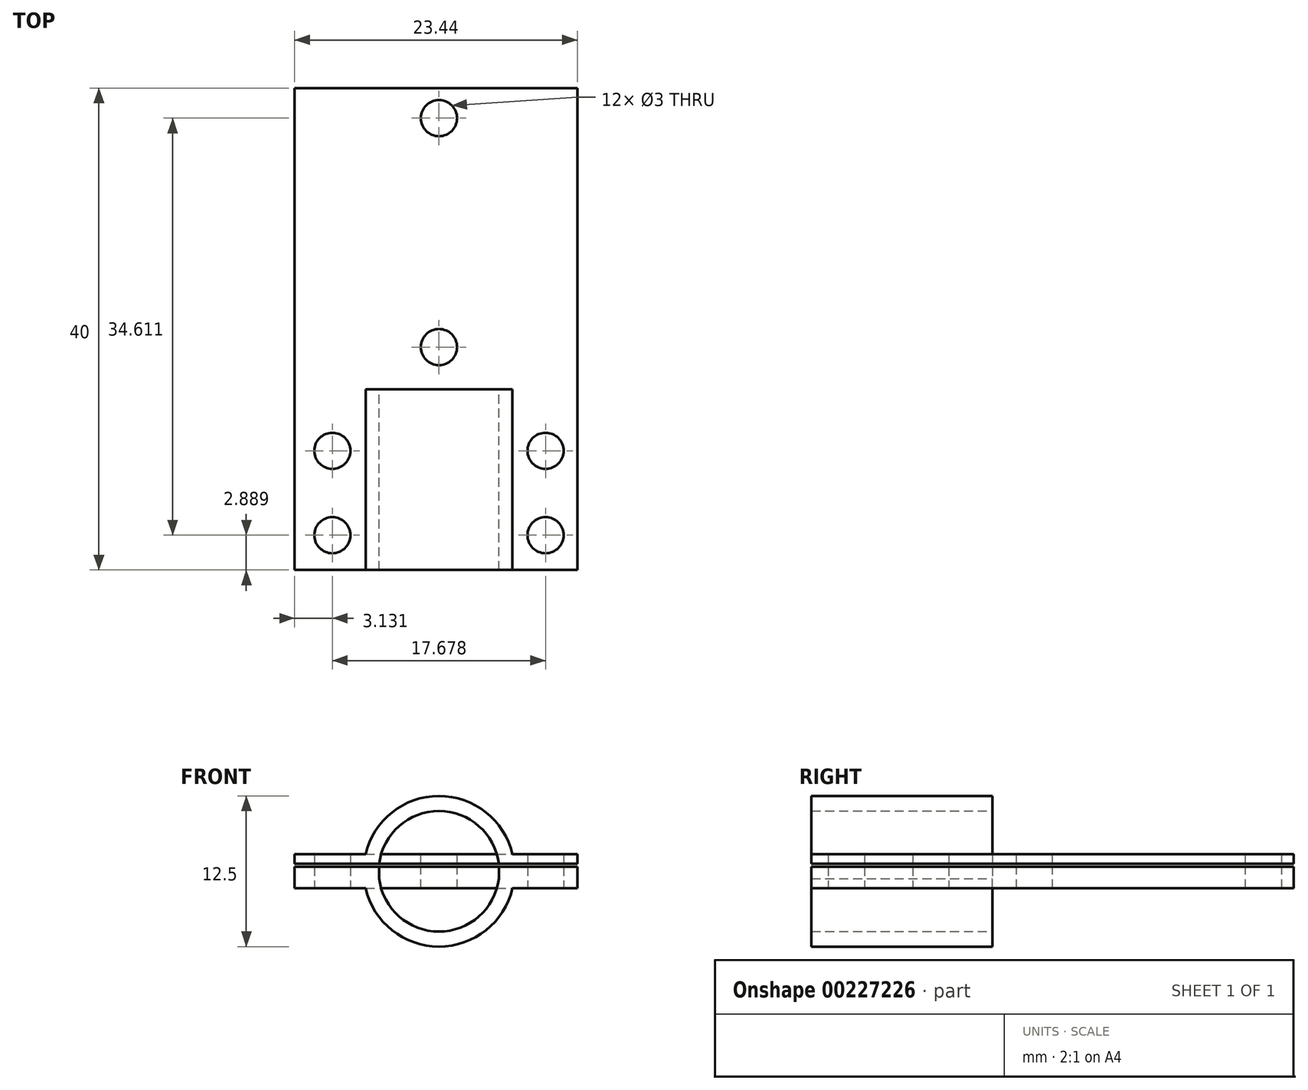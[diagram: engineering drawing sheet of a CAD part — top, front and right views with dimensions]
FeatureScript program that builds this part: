
annotation { "Feature Type Name" : "Feature", "Feature Type Description" : "" }
export const myFeature = defineFeature(function(context is Context, id is Id, definition is map)
    precondition{}
    {
        {
            var Q0;
            Q0=qCreatedBy(makeId("Front.planeOp"),FACE);
            var sketch = newSketch(context, id + "F0", { "sketchPlane" : qUnion([Q0])});
            skCircle(sketch, "E0", {"center": v(0, 0) * mm, "radius": 5 * mm});
            skArc(sketch, "E1", {"start": v(-6.09, -1.4) * mm, "mid": v(0, -6.25) * mm, "end": v(6.09, -1.4) * mm});
            skLineSegment(sketch, "E2.bottom", {"start": v(9.47, -1.4) * mm, "end": v(4.8, -1.4) * mm});
            skLineSegment(sketch, "E2.top", {"start": v(9.47, 1.4) * mm, "end": v(4.8, 1.4) * mm});
            skLineSegment(sketch, "E2.left", {"start": v(9.47, -1.4) * mm, "end": v(9.47, 1.4) * mm});
            skLineSegment(sketch, "E2.right", {"start": v(-9.47, -1.4) * mm, "end": v(-9.47, 1.4) * mm});
            skArc(sketch, "E3.trimOffspring", {"start": v(6.09, 1.4) * mm, "mid": v(0, 6.25) * mm, "end": v(-6.09, 1.4) * mm});
            skLineSegment(sketch, "E4.bottom", {"start": v(8.3, -0.63) * mm, "end": v(4.96, -0.63) * mm});
            skLineSegment(sketch, "E4.top", {"start": v(8.3, 0.63) * mm, "end": v(4.96, 0.63) * mm});
            skLineSegment(sketch, "E4.left", {"start": v(8.3, -0.63) * mm, "end": v(8.3, 0.63) * mm});
            skLineSegment(sketch, "E4.right", {"start": v(-8.3, -0.63) * mm, "end": v(-8.3, 0.63) * mm});
            skLineSegment(sketch, "E5.trimOffspring", {"start": v(-4.8, 1.4) * mm, "end": v(-9.47, 1.4) * mm});
            skLineSegment(sketch, "E6.trimOffspring", {"start": v(-4.96, 0.63) * mm, "end": v(-8.3, 0.63) * mm});
            skLineSegment(sketch, "E7.trimOffspring", {"start": v(-4.96, -0.63) * mm, "end": v(-8.3, -0.63) * mm});
            skLineSegment(sketch, "E8.trimOffspring", {"start": v(-4.8, -1.4) * mm, "end": v(-9.47, -1.4) * mm});
            skSolve(sketch);
        }
        {
            var Q0;
            Q0 = qSketchRegion(id + "F0", true);
            extrude(context, id + "F1", {"entities" : qUnion([Q0]), "endBound" : BoundingType.SYMMETRIC, "depth" : 25 * mm});
        }
        {
            var Q0;
            Q0=makeQuery(id+"F1.opExtrude","SWEPT_FACE",FACE,{"disambiguationData":[OSD([sQuery(id+"F0.wireOp",EDGE,"E5.trimOffspring")])]});
            var sketch = newSketch(context, id + "F2", { "sketchPlane" : qUnion([Q0])});
            skLineSegment(sketch, "E9", {"start": v(-9.47, 0) * mm, "end": v(9.47, 0) * mm});
            skPoint(sketch, "E9.endSnap0", {"position": v(-9.47, 0) * mm});
            skLineSegment(sketch, "E10", {"start": v(9.47, 0) * mm, "end": v(9.47, 12.5) * mm});
            skLineSegment(sketch, "E11", {"start": v(9.47, 12.5) * mm, "end": v(-9.47, 12.5) * mm});
            skLineSegment(sketch, "E12", {"start": v(-9.47, 12.5) * mm, "end": v(-9.47, 0) * mm});
            skSolve(sketch);
        }
        {
            var Q0;
            Q0 = qSketchRegion(id + "F2", true);
            extrude(context, id + "F3", {"entities" : qUnion([Q0]), "operationType" : NewBodyOperationType.ADD, "depth" : 5.1 * mm});
        }
        {
            var Q0;
            {var subQ3=sQuery(id+"F2.wireOp",EDGE,"E9");Q0=makeQuery(id+"F3.boolean.opBoolean","SPLIT",FACE,{"disambiguationData":[TD([makeQuery(id+"F3.opExtrude","CAP_FACE",FACE,{"disambiguationData":[OSD([subQ3,sQuery(id+"F2.wireOp",EDGE,"E10"),sQuery(id+"F2.wireOp",EDGE,"E11"),sQuery(id+"F2.wireOp",EDGE,"E12")])],"isStart":true})])],"derivedFrom":makeQuery(id+"F3.opExtrude","SWEPT_FACE",FACE,{"disambiguationData":[OSD([subQ3])]})});}
            extrude(context, id + "F4", {"entities" : qUnion([Q0]), "operationType" : NewBodyOperationType.REMOVE, "oppositeDirection" : true, "depth" : 25 * mm});
        }
        {
            var Q0;
            Q0=makeQuery(id+"F3.opExtrude","CAP_FACE",FACE,{"disambiguationData":[OSD([sQuery(id+"F2.wireOp",EDGE,"E9"),sQuery(id+"F2.wireOp",EDGE,"E10"),sQuery(id+"F2.wireOp",EDGE,"E11"),sQuery(id+"F2.wireOp",EDGE,"E12")])],"isStart":false});
            extrude(context, id + "F5", {"entities" : qUnion([Q0]), "operationType" : NewBodyOperationType.ADD, "oppositeDirection" : true, "depth" : 13 * mm});
        }
        {
            var Q0;
            {var subQ6=sQuery(id+"F0.wireOp",EDGE,"E4.bottom");var subQ9=sQuery(id+"F2.wireOp",EDGE,"E9");Q0=makeQuery(id+"F5.boolean.opBoolean","SPLIT",FACE,{"disambiguationData":[TD([makeQuery(id+"F1.opExtrude","SWEPT_FACE",FACE,{"disambiguationData":[OSD([subQ6])]})])],"derivedFrom":makeQuery(id+"F5.opExtrude","SWEPT_FACE",FACE,{"disambiguationData":[OSD([subQ9])]})});}
            extrude(context, id + "F6", {"entities" : qUnion([Q0]), "operationType" : NewBodyOperationType.REMOVE, "oppositeDirection" : true, "depth" : 3 * mm});
        }
        {
            var Q0;
            Q0=makeQuery(id+"F1.opExtrude","SWEPT_FACE",FACE,{"disambiguationData":[OSD([sQuery(id+"F0.wireOp",EDGE,"E2.bottom")])]});
            var sketch = newSketch(context, id + "F7", { "sketchPlane" : qUnion([Q0])});
            skCircle(sketch, "E13", {"center": v(8.84, 9.61) * mm, "radius": 1.5 * mm});
            skCircle(sketch, "E14.0.1.0", {"center": v(8.84, 2.61) * mm, "radius": 1.5 * mm});
            skLineSegment(sketch, "E14.direction1", {"start": v(8.84, 9.61) * mm, "end": v(33.84, 9.61) * mm, "construction": true});
            skLineSegment(sketch, "E14.direction2", {"start": v(8.84, 9.61) * mm, "end": v(8.84, 2.61) * mm, "construction": true});
            skCircle(sketch, "E15.MirrorC", {"center": v(-8.84, 9.61) * mm, "radius": 1.5 * mm});
            skCircle(sketch, "E16.MirrorC", {"center": v(-8.84, 2.61) * mm, "radius": 1.5 * mm});
            skSolve(sketch);
        }
        {
            var Q0;
            Q0=makeQuery(id+"F1.opExtrude","SWEPT_FACE",FACE,{"disambiguationData":[OSD([sQuery(id+"F0.wireOp",EDGE,"E2.left")])]});
            extrude(context, id + "F8", {"entities" : qUnion([Q0]), "operationType" : NewBodyOperationType.ADD, "depth" : 2 * mm});
        }
        {
            var Q0;
            {var subQ0=sQuery(id+"F0.wireOp",EDGE,"E4.left");Q0=makeQuery(id+"F6.boolean.opBoolean","MERGE",FACE,{"derivedFrom":[makeQuery(id+"F1.opExtrude","SWEPT_FACE",FACE,{"disambiguationData":[OSD([subQ0])]}),makeQuery(id+"F6.opExtrude","SWEPT_FACE",FACE,{"disambiguationData":[OSD([subQ0,sQuery(id+"F2.wireOp",EDGE,"E9")])]})]});}
            extrude(context, id + "F9", {"entities" : qUnion([Q0]), "operationType" : NewBodyOperationType.REMOVE, "oppositeDirection" : true, "depth" : 23.6 * mm});
        }
        {
            var Q0;
            {var subQ0=sQuery(id+"F2.wireOp",EDGE,"E12");Q0=makeQuery(id+"F5.boolean.opBoolean","MERGE",FACE,{"derivedFrom":[makeQuery(id+"F3.boolean.opBoolean","MERGE",FACE,{"derivedFrom":[makeQuery(id+"F1.opExtrude","SWEPT_FACE",FACE,{"disambiguationData":[OSD([sQuery(id+"F0.wireOp",EDGE,"E2.right")])]}),makeQuery(id+"F3.opExtrude","SWEPT_FACE",FACE,{"disambiguationData":[OSD([subQ0])]})]}),makeQuery(id+"F5.opExtrude","SWEPT_FACE",FACE,{"disambiguationData":[OSD([subQ0])]})]});}
            var sketch = newSketch(context, id + "F10", { "sketchPlane" : qUnion([Q0])});
            skLineSegment(sketch, "E17", {"start": v(0, -1.4) * mm, "end": v(0, 1.4) * mm});
            skSolve(sketch);
        }
        {
            var Q0;
            Q0 = qSketchRegion(id + "F10", true);
            var Q1;
            Q1=makeQuery(id+"F10.imprint","IMPRINT",FACE,{"disambiguationData":[TD([[makeQuery(id+"F10.imprint","IMPRINT",EDGE,{"derivedFrom":sQuery(id+"F10.wireOp",EDGE,"E17")}),-1.0]])]});
            extrude(context, id + "F11", {"entities" : qUnion([Q0, Q1]), "operationType" : NewBodyOperationType.ADD, "depth" : 2.5 * mm});
        }
        {
            var Q0;
            {var subQ0=sQuery(id+"F0.wireOp",EDGE,"E4.right");Q0=makeQuery(id+"F6.boolean.opBoolean","MERGE",FACE,{"derivedFrom":[makeQuery(id+"F1.opExtrude","SWEPT_FACE",FACE,{"disambiguationData":[OSD([subQ0])]}),makeQuery(id+"F6.opExtrude","SWEPT_FACE",FACE,{"disambiguationData":[OSD([subQ0,sQuery(id+"F2.wireOp",EDGE,"E9")])]})]});}
            extrude(context, id + "F12", {"entities" : qUnion([Q0]), "operationType" : NewBodyOperationType.REMOVE, "oppositeDirection" : true, "depth" : 2.5 * mm});
        }
        {
            var Q0;
            Q0=makeQuery(id+"F11.opExtrude","SWEPT_FACE",FACE,{"disambiguationData":[OSD([sQuery(id+"F10.wireOp",EDGE,"E17")])]});
            extrude(context, id + "F13", {"entities" : qUnion([Q0]), "operationType" : NewBodyOperationType.ADD, "depth" : 12.5 * mm});
        }
        {
            var Q0;
            {var subQ4=sQuery(id+"F0.wireOp",EDGE,"E6.trimOffspring");var subQ7=sQuery(id+"F0.wireOp",EDGE,"E2.right");var subQ9=sQuery(id+"F2.wireOp",EDGE,"E12");Q0=makeQuery(id+"F13.boolean.opBoolean","SPLIT",FACE,{"disambiguationData":[TD([makeQuery(id+"F1.opExtrude","SWEPT_FACE",FACE,{"disambiguationData":[OSD([subQ4])]})])],"derivedFrom":makeQuery(id+"F5.boolean.opBoolean","MERGE",FACE,{"derivedFrom":[makeQuery(id+"F3.boolean.opBoolean","MERGE",FACE,{"derivedFrom":[makeQuery(id+"F1.opExtrude","SWEPT_FACE",FACE,{"disambiguationData":[OSD([subQ7])]}),makeQuery(id+"F3.opExtrude","SWEPT_FACE",FACE,{"disambiguationData":[OSD([subQ9])]})]}),makeQuery(id+"F5.opExtrude","SWEPT_FACE",FACE,{"disambiguationData":[OSD([subQ9])]})]})});}
            extrude(context, id + "F14", {"entities" : qUnion([Q0]), "operationType" : NewBodyOperationType.ADD, "depth" : 2 * mm});
        }
        {
            var Q0;
            Q0 = qSketchRegion(id + "F7", true);
            extrude(context, id + "F15", {"entities" : qUnion([Q0]), "operationType" : NewBodyOperationType.REMOVE, "oppositeDirection" : true, "depth" : 25 * mm});
        }
        {
            var Q0;
            {var subQ2=sQuery(id+"F2.wireOp",EDGE,"E9");Q0=makeQuery(id+"F5.boolean.opBoolean","SPLIT",FACE,{"disambiguationData":[TD([makeQuery(id+"F1.opExtrude","SWEPT_FACE",FACE,{"disambiguationData":[OSD([sQuery(id+"F0.wireOp",EDGE,"E1")])]})])],"derivedFrom":makeQuery(id+"F5.opExtrude","SWEPT_FACE",FACE,{"disambiguationData":[OSD([subQ2])]})});}
            var Q1;
            {var subQ2=sQuery(id+"F2.wireOp",EDGE,"E9");Q1=makeQuery(id+"F3.boolean.opBoolean","SPLIT",FACE,{"disambiguationData":[TD([makeQuery(id+"F1.opExtrude","SWEPT_FACE",FACE,{"disambiguationData":[OSD([sQuery(id+"F0.wireOp",EDGE,"E2.top")])]})])],"derivedFrom":makeQuery(id+"F3.opExtrude","SWEPT_FACE",FACE,{"disambiguationData":[OSD([subQ2])]})});}
            extrude(context, id + "F16", {"entities" : qUnion([Q0, Q1]), "operationType" : NewBodyOperationType.REMOVE, "oppositeDirection" : true, "depth" : 2 * mm});
        }
        {
            var Q0;
            {var subQ0=sQuery(id+"F2.wireOp",EDGE,"E9");var subQ1=sQuery(id+"F0.wireOp",EDGE,"E4.right");Q0=makeQuery(id+"F13.boolean.opBoolean","MERGE",FACE,{"derivedFrom":[makeQuery(id+"F12.boolean.opBoolean","COPY",FACE,{"derivedFrom":makeQuery(id+"F12.opExtrude","CAP_FACE",FACE,{"disambiguationData":[OSD([subQ1,subQ0])],"isStart":false})}),makeQuery(id+"F13.opExtrude","SWEPT_FACE",FACE,{"disambiguationData":[OSD([subQ1,subQ0,sQuery(id+"F10.wireOp",EDGE,"E17")])]})]});}
            extrude(context, id + "F17", {"entities" : qUnion([Q0]), "operationType" : NewBodyOperationType.REMOVE, "oppositeDirection" : true, "depth" : 12 * mm});
        }
        {
            var Q0;
            {var subQ0=sQuery(id+"F2.wireOp",EDGE,"E12");var subQ1=sQuery(id+"F2.wireOp",EDGE,"E9");var subQ2=sQuery(id+"F0.wireOp",EDGE,"E4.right");var subQ3=sQuery(id+"F0.wireOp",EDGE,"E2.right");Q0=makeQuery(id+"F17.boolean.opBoolean","MERGE",FACE,{"derivedFrom":[makeQuery(id+"F14.boolean.opBoolean","MERGE",FACE,{"derivedFrom":[makeQuery(id+"F12.boolean.opBoolean","MERGE",FACE,{"derivedFrom":[makeQuery(id+"F9.boolean.opBoolean","MERGE",FACE,{"derivedFrom":[makeQuery(id+"F6.boolean.opBoolean","COPY",FACE,{"derivedFrom":makeQuery(id+"F6.opExtrude","CAP_FACE",FACE,{"disambiguationData":[OSD([subQ1])],"isStart":false})}),makeQuery(id+"F9.opExtrude","SWEPT_FACE",FACE,{"disambiguationData":[OSD([sQuery(id+"F0.wireOp",EDGE,"E4.left"),subQ1])]})]}),makeQuery(id+"F12.opExtrude","SWEPT_FACE",FACE,{"disambiguationData":[OSD([subQ2,subQ1])]})]}),makeQuery(id+"F14.opExtrude","SWEPT_FACE",FACE,{"disambiguationData":[OSD([subQ3,subQ2,subQ1,subQ0])]})]}),makeQuery(id+"F17.opExtrude","SWEPT_FACE",FACE,{"disambiguationData":[OSD([subQ3,subQ2,subQ1,subQ0,sQuery(id+"F10.wireOp",EDGE,"E17")])]})]});}
            extrude(context, id + "F18", {"entities" : qUnion([Q0]), "operationType" : NewBodyOperationType.REMOVE, "oppositeDirection" : true, "depth" : 25 * mm});
        }
        {
            var Q0;
            {var subQ2=sQuery(id+"F2.wireOp",EDGE,"E9");Q0=makeQuery(id+"F16.boolean.opBoolean","COPY",FACE,{"derivedFrom":makeQuery(id+"F16.opExtrude","CAP_FACE",FACE,{"disambiguationData":[OSD([subQ2]),TDD([makeQuery(id+"F5.boolean.opBoolean","SPLIT",FACE,{"disambiguationData":[TD([makeQuery(id+"F1.opExtrude","SWEPT_FACE",FACE,{"disambiguationData":[OSD([sQuery(id+"F0.wireOp",EDGE,"E1")])]})])],"derivedFrom":makeQuery(id+"F5.opExtrude","SWEPT_FACE",FACE,{"disambiguationData":[OSD([subQ2])]})})])],"isStart":false})});}
            extrude(context, id + "F19", {"entities" : qUnion([Q0]), "operationType" : NewBodyOperationType.REMOVE, "oppositeDirection" : true, "depth" : 25 * mm});
        }
        {
            var Q0;
            {var subQ2=sQuery(id+"F2.wireOp",EDGE,"E9");Q0=makeQuery(id+"F16.boolean.opBoolean","COPY",FACE,{"derivedFrom":makeQuery(id+"F16.opExtrude","CAP_FACE",FACE,{"disambiguationData":[OSD([subQ2]),TDD([makeQuery(id+"F3.boolean.opBoolean","SPLIT",FACE,{"disambiguationData":[TD([makeQuery(id+"F1.opExtrude","SWEPT_FACE",FACE,{"disambiguationData":[OSD([sQuery(id+"F0.wireOp",EDGE,"E2.top")])]})])],"derivedFrom":makeQuery(id+"F3.opExtrude","SWEPT_FACE",FACE,{"disambiguationData":[OSD([subQ2])]})})])],"isStart":false})});}
            extrude(context, id + "F20", {"entities" : qUnion([Q0]), "operationType" : NewBodyOperationType.REMOVE, "oppositeDirection" : true, "depth" : 25 * mm});
        }
        {
            var Q0;
            {var subQ0=sQuery(id+"F10.wireOp",EDGE,"E17");var subQ1=sQuery(id+"F2.wireOp",EDGE,"E9");var subQ2=sQuery(id+"F0.wireOp",EDGE,"E7.trimOffspring");var subQ3=sQuery(id+"F0.wireOp",EDGE,"E4.right");Q0=makeQuery(id+"F18.boolean.opBoolean","MERGE",FACE,{"derivedFrom":[makeQuery(id+"F17.boolean.opBoolean","MERGE",FACE,{"derivedFrom":[makeQuery(id+"F13.boolean.opBoolean","MERGE",FACE,{"derivedFrom":[makeQuery(id+"F12.boolean.opBoolean","MERGE",FACE,{"derivedFrom":[makeQuery(id+"F6.boolean.opBoolean","MERGE",FACE,{"derivedFrom":[makeQuery(id+"F1.opExtrude","SWEPT_FACE",FACE,{"disambiguationData":[OSD([subQ2])]}),makeQuery(id+"F6.opExtrude","SWEPT_FACE",FACE,{"disambiguationData":[OSD([subQ2,subQ1])]})]}),makeQuery(id+"F12.opExtrude","SWEPT_FACE",FACE,{"disambiguationData":[OSD([subQ3,subQ2,subQ1])]})]}),makeQuery(id+"F13.opExtrude","SWEPT_FACE",FACE,{"disambiguationData":[OSD([subQ3,subQ2,subQ1,subQ0])]})]}),makeQuery(id+"F17.opExtrude","SWEPT_FACE",FACE,{"disambiguationData":[OSD([subQ3,subQ2,subQ1,subQ0])]})]}),makeQuery(id+"F18.opExtrude","SWEPT_FACE",FACE,{"disambiguationData":[OSD([sQuery(id+"F0.wireOp",EDGE,"E2.right"),subQ3,subQ2,subQ1,sQuery(id+"F2.wireOp",EDGE,"E12"),subQ0])]})]});}
            extrude(context, id + "F21", {"entities" : qUnion([Q0]), "operationType" : NewBodyOperationType.ADD, "depth" : 1 * mm});
        }
        {
            var Q0;
            {var subQ0=sQuery(id+"F2.wireOp",EDGE,"E9");var subQ1=sQuery(id+"F0.wireOp",EDGE,"E4.left");var subQ2=sQuery(id+"F0.wireOp",EDGE,"E4.bottom");Q0=makeQuery(id+"F18.boolean.opBoolean","MERGE",FACE,{"derivedFrom":[makeQuery(id+"F9.boolean.opBoolean","MERGE",FACE,{"derivedFrom":[makeQuery(id+"F6.boolean.opBoolean","MERGE",FACE,{"derivedFrom":[makeQuery(id+"F1.opExtrude","SWEPT_FACE",FACE,{"disambiguationData":[OSD([subQ2])]}),makeQuery(id+"F6.opExtrude","SWEPT_FACE",FACE,{"disambiguationData":[OSD([subQ2,subQ0])]})]}),makeQuery(id+"F9.opExtrude","SWEPT_FACE",FACE,{"disambiguationData":[OSD([subQ2,subQ1,subQ0])]})]}),makeQuery(id+"F18.opExtrude","SWEPT_FACE",FACE,{"disambiguationData":[OSD([subQ2,subQ1,subQ0])]})]});}
            extrude(context, id + "F22", {"entities" : qUnion([Q0]), "operationType" : NewBodyOperationType.ADD, "depth" : 1 * mm});
        }
        {
            var Q0;
            {var subQ0=sQuery(id+"F10.wireOp",EDGE,"E17");var subQ1=sQuery(id+"F2.wireOp",EDGE,"E12");var subQ2=sQuery(id+"F2.wireOp",EDGE,"E11");var subQ3=sQuery(id+"F2.wireOp",EDGE,"E9");var subQ4=sQuery(id+"F0.wireOp",EDGE,"E8.trimOffspring");var subQ5=sQuery(id+"F0.wireOp",EDGE,"E7.trimOffspring");var subQ6=sQuery(id+"F0.wireOp",EDGE,"E6.trimOffspring");var subQ7=sQuery(id+"F0.wireOp",EDGE,"E5.trimOffspring");var subQ8=sQuery(id+"F0.wireOp",EDGE,"E4.right");var subQ9=sQuery(id+"F0.wireOp",EDGE,"E4.left");var subQ10=sQuery(id+"F0.wireOp",EDGE,"E4.top");var subQ11=sQuery(id+"F0.wireOp",EDGE,"E4.bottom");var subQ12=sQuery(id+"F0.wireOp",EDGE,"E3.trimOffspring");var subQ13=sQuery(id+"F0.wireOp",EDGE,"E2.right");var subQ14=sQuery(id+"F0.wireOp",EDGE,"E2.left");var subQ15=sQuery(id+"F0.wireOp",EDGE,"E2.top");var subQ16=sQuery(id+"F0.wireOp",EDGE,"E2.bottom");var subQ17=sQuery(id+"F0.wireOp",EDGE,"E1");var subQ18=sQuery(id+"F0.wireOp",EDGE,"E0");Q0=makeQuery(id+"F22.boolean.opBoolean","MERGE",FACE,{"derivedFrom":[makeQuery(id+"F21.boolean.opBoolean","MERGE",FACE,{"derivedFrom":[makeQuery(id+"F18.boolean.opBoolean","SPLIT",FACE,{"disambiguationData":[TD([makeQuery(id+"F1.opExtrude","SWEPT_FACE",FACE,{"disambiguationData":[OSD([subQ16])]})])],"derivedFrom":makeQuery(id+"F14.boolean.opBoolean","MERGE",FACE,{"derivedFrom":[makeQuery(id+"F13.boolean.opBoolean","MERGE",FACE,{"derivedFrom":[makeQuery(id+"F8.boolean.opBoolean","MERGE",FACE,{"derivedFrom":[makeQuery(id+"F5.boolean.opBoolean","MERGE",FACE,{"derivedFrom":[makeQuery(id+"F3.boolean.opBoolean","MERGE",FACE,{"derivedFrom":[makeQuery(id+"F1.opExtrude","CAP_FACE",FACE,{"disambiguationData":[OSD([subQ18,subQ17,subQ16,subQ15,subQ14,subQ13,subQ12,subQ11,subQ10,subQ9,subQ8,subQ7,subQ6,subQ5,subQ4])],"isStart":true}),makeQuery(id+"F3.opExtrude","SWEPT_FACE",FACE,{"disambiguationData":[OSD([subQ2])]})]}),makeQuery(id+"F5.opExtrude","SWEPT_FACE",FACE,{"disambiguationData":[OSD([subQ2])]})]}),makeQuery(id+"F8.opExtrude","SWEPT_FACE",FACE,{"disambiguationData":[OSD([subQ14]),TDD([makeQuery(id+"F1.opExtrude","CAP_EDGE",EDGE,{"disambiguationData":[OSD([subQ14])],"isStart":true})])]})]}),makeQuery(id+"F13.opExtrude","CAP_FACE",FACE,{"disambiguationData":[OSD([subQ0])],"isStart":false})]}),makeQuery(id+"F14.opExtrude","SWEPT_FACE",FACE,{"disambiguationData":[OSD([subQ13,subQ2,subQ1])]})]})}),makeQuery(id+"F21.opExtrude","SWEPT_FACE",FACE,{"disambiguationData":[OSD([subQ18,subQ17,subQ16,subQ15,subQ14,subQ13,subQ12,subQ11,subQ10,subQ9,subQ8,subQ7,subQ6,subQ5,subQ4,subQ3,subQ2,subQ1,subQ0])]})]}),makeQuery(id+"F22.opExtrude","SWEPT_FACE",FACE,{"disambiguationData":[OSD([subQ18,subQ17,subQ16,subQ15,subQ14,subQ13,subQ12,subQ11,subQ10,subQ9,subQ8,subQ7,subQ6,subQ5,subQ4,subQ3,subQ2,subQ1,subQ0])]})]});}
            var Q1;
            {var subQ0=sQuery(id+"F10.wireOp",EDGE,"E17");var subQ1=sQuery(id+"F0.wireOp",EDGE,"E8.trimOffspring");var subQ2=sQuery(id+"F0.wireOp",EDGE,"E5.trimOffspring");var subQ3=sQuery(id+"F0.wireOp",EDGE,"E2.right");var subQ5=sQuery(id+"F0.wireOp",EDGE,"E2.left");var subQ6=sQuery(id+"F0.wireOp",EDGE,"E2.top");var subQ8=sQuery(id+"F0.wireOp",EDGE,"E0");var subQ11=sQuery(id+"F0.wireOp",EDGE,"E6.trimOffspring");var subQ13=sQuery(id+"F0.wireOp",EDGE,"E4.top");var subQ16=sQuery(id+"F2.wireOp",EDGE,"E12");var subQ18=sQuery(id+"F0.wireOp",EDGE,"E4.right");var subQ19=makeQuery(id+"F1.opExtrude","SWEPT_FACE",FACE,{"disambiguationData":[OSD([subQ6])]});var subQ20=sQuery(id+"F2.wireOp",EDGE,"E11");var subQ21=sQuery(id+"F0.wireOp",EDGE,"E4.left");Q1=makeQuery(id+"F18.boolean.opBoolean","SPLIT",FACE,{"disambiguationData":[TD([subQ19])],"derivedFrom":makeQuery(id+"F14.boolean.opBoolean","MERGE",FACE,{"derivedFrom":[makeQuery(id+"F13.boolean.opBoolean","MERGE",FACE,{"derivedFrom":[makeQuery(id+"F8.boolean.opBoolean","MERGE",FACE,{"derivedFrom":[makeQuery(id+"F5.boolean.opBoolean","MERGE",FACE,{"derivedFrom":[makeQuery(id+"F3.boolean.opBoolean","MERGE",FACE,{"derivedFrom":[makeQuery(id+"F1.opExtrude","CAP_FACE",FACE,{"disambiguationData":[OSD([subQ8,sQuery(id+"F0.wireOp",EDGE,"E1"),sQuery(id+"F0.wireOp",EDGE,"E2.bottom"),subQ6,subQ5,subQ3,sQuery(id+"F0.wireOp",EDGE,"E3.trimOffspring"),sQuery(id+"F0.wireOp",EDGE,"E4.bottom"),subQ13,subQ21,subQ18,subQ2,subQ11,sQuery(id+"F0.wireOp",EDGE,"E7.trimOffspring"),subQ1])],"isStart":true}),makeQuery(id+"F3.opExtrude","SWEPT_FACE",FACE,{"disambiguationData":[OSD([subQ20])]})]}),makeQuery(id+"F5.opExtrude","SWEPT_FACE",FACE,{"disambiguationData":[OSD([subQ20])]})]}),makeQuery(id+"F8.opExtrude","SWEPT_FACE",FACE,{"disambiguationData":[OSD([subQ5]),TDD([makeQuery(id+"F1.opExtrude","CAP_EDGE",EDGE,{"disambiguationData":[OSD([subQ5])],"isStart":true})])]})]}),makeQuery(id+"F13.opExtrude","CAP_FACE",FACE,{"disambiguationData":[OSD([subQ0])],"isStart":false})]}),makeQuery(id+"F14.opExtrude","SWEPT_FACE",FACE,{"disambiguationData":[OSD([subQ3,subQ20,subQ16])]})]})});}
            extrude(context, id + "F23", {"entities" : qUnion([Q0, Q1]), "operationType" : NewBodyOperationType.REMOVE, "oppositeDirection" : true, "depth" : 10 * mm});
        }
        {
            var Q0;
            Q0=makeQuery(id+"F23.boolean.opBoolean","COPY",FACE,{"derivedFrom":makeQuery(id+"F23.opExtrude","CAP_FACE",FACE,{"disambiguationData":[OSD([sQuery(id+"F0.wireOp",EDGE,"E0"),sQuery(id+"F0.wireOp",EDGE,"E1"),sQuery(id+"F0.wireOp",EDGE,"E2.bottom"),sQuery(id+"F0.wireOp",EDGE,"E2.top"),sQuery(id+"F0.wireOp",EDGE,"E2.left"),sQuery(id+"F0.wireOp",EDGE,"E2.right"),sQuery(id+"F0.wireOp",EDGE,"E3.trimOffspring"),sQuery(id+"F0.wireOp",EDGE,"E4.bottom"),sQuery(id+"F0.wireOp",EDGE,"E4.top"),sQuery(id+"F0.wireOp",EDGE,"E4.left"),sQuery(id+"F0.wireOp",EDGE,"E4.right"),sQuery(id+"F0.wireOp",EDGE,"E5.trimOffspring"),sQuery(id+"F0.wireOp",EDGE,"E6.trimOffspring"),sQuery(id+"F0.wireOp",EDGE,"E7.trimOffspring"),sQuery(id+"F0.wireOp",EDGE,"E8.trimOffspring"),sQuery(id+"F2.wireOp",EDGE,"E9"),sQuery(id+"F2.wireOp",EDGE,"E11"),sQuery(id+"F2.wireOp",EDGE,"E12"),sQuery(id+"F10.wireOp",EDGE,"E17")])],"isStart":false})});
            var sketch = newSketch(context, id + "F24", { "sketchPlane" : qUnion([Q0])});
            skLineSegment(sketch, "E18.bottom", {"start": v(11.97, 0.37) * mm, "end": v(-11.47, 0.37) * mm});
            skLineSegment(sketch, "E18.top", {"start": v(11.97, -1.4) * mm, "end": v(-11.47, -1.4) * mm});
            skLineSegment(sketch, "E18.left", {"start": v(11.97, 0.37) * mm, "end": v(11.97, -1.4) * mm});
            skLineSegment(sketch, "E18.right", {"start": v(-11.47, 0.37) * mm, "end": v(-11.47, -1.4) * mm});
            skSolve(sketch);
        }
        {
            var Q0;
            Q0 = qSketchRegion(id + "F24", true);
            extrude(context, id + "F25", {"entities" : qUnion([Q0]), "operationType" : NewBodyOperationType.ADD, "depth" : 25 * mm});
        }
        {
            var Q0;
            Q0=makeQuery(id+"F23.boolean.opBoolean","COPY",FACE,{"derivedFrom":makeQuery(id+"F23.opExtrude","CAP_FACE",FACE,{"disambiguationData":[OSD([sQuery(id+"F0.wireOp",EDGE,"E0"),sQuery(id+"F0.wireOp",EDGE,"E1"),sQuery(id+"F0.wireOp",EDGE,"E2.bottom"),sQuery(id+"F0.wireOp",EDGE,"E2.top"),sQuery(id+"F0.wireOp",EDGE,"E2.left"),sQuery(id+"F0.wireOp",EDGE,"E2.right"),sQuery(id+"F0.wireOp",EDGE,"E3.trimOffspring"),sQuery(id+"F0.wireOp",EDGE,"E4.bottom"),sQuery(id+"F0.wireOp",EDGE,"E4.top"),sQuery(id+"F0.wireOp",EDGE,"E4.left"),sQuery(id+"F0.wireOp",EDGE,"E4.right"),sQuery(id+"F0.wireOp",EDGE,"E5.trimOffspring"),sQuery(id+"F0.wireOp",EDGE,"E6.trimOffspring"),sQuery(id+"F0.wireOp",EDGE,"E7.trimOffspring"),sQuery(id+"F0.wireOp",EDGE,"E8.trimOffspring"),sQuery(id+"F2.wireOp",EDGE,"E11"),sQuery(id+"F2.wireOp",EDGE,"E12"),sQuery(id+"F10.wireOp",EDGE,"E17")])],"isStart":false})});
            var sketch = newSketch(context, id + "F26", { "sketchPlane" : qUnion([Q0])});
            skLineSegment(sketch, "E19.bottom", {"start": v(11.97, 0.63) * mm, "end": v(-11.47, 0.63) * mm});
            skLineSegment(sketch, "E19.top", {"start": v(11.97, 1.4) * mm, "end": v(-11.47, 1.4) * mm});
            skLineSegment(sketch, "E19.left", {"start": v(11.97, 0.63) * mm, "end": v(11.97, 1.4) * mm});
            skLineSegment(sketch, "E19.right", {"start": v(-11.47, 0.63) * mm, "end": v(-11.47, 1.4) * mm});
            skSolve(sketch);
        }
        {
            var Q0;
            Q0 = qSketchRegion(id + "F26", true);
            extrude(context, id + "F27", {"entities" : qUnion([Q0]), "operationType" : NewBodyOperationType.ADD, "depth" : 25 * mm});
        }
        {
            var Q0;
            {var subQ0=sQuery(id+"F0.wireOp",EDGE,"E5.trimOffspring");var subQ1=makeQuery(id+"F1.opExtrude","SWEPT_FACE",FACE,{"disambiguationData":[OSD([subQ0])]});var subQ2=sQuery(id+"F2.wireOp",EDGE,"E9");var subQ4=makeQuery(id+"F3.opExtrude","CAP_EDGE",EDGE,{"disambiguationData":[OSD([subQ2])],"isStart":true});var subQ5=makeQuery(id+"F3.boolean.opBoolean","SPLIT",EDGE,{"disambiguationData":[topologyDisambiguationEdgeConnected([subQ1])],"derivedFrom":subQ4});var subQ6=sQuery(id+"F0.wireOp",EDGE,"E2.right");var subQ7=sQuery(id+"F0.wireOp",EDGE,"E2.top");var subQ8=makeQuery(id+"F1.opExtrude","SWEPT_FACE",FACE,{"disambiguationData":[OSD([subQ7])]});var subQ9=makeQuery(id+"F3.boolean.opBoolean","SPLIT",EDGE,{"disambiguationData":[topologyDisambiguationEdgeConnected([subQ8])],"derivedFrom":subQ4});Q0=makeQuery(id+"F27.boolean.opBoolean","MERGE",FACE,{"derivedFrom":[makeQuery(id+"F20.boolean.opBoolean","MERGE",FACE,{"derivedFrom":[makeQuery(id+"F16.boolean.opBoolean","MERGE",FACE,{"derivedFrom":[makeQuery(id+"F8.boolean.opBoolean","MERGE",FACE,{"derivedFrom":[subQ8,makeQuery(id+"F8.opExtrude","SWEPT_FACE",FACE,{"disambiguationData":[OSD([subQ7,sQuery(id+"F0.wireOp",EDGE,"E2.left"),sQuery(id+"F2.wireOp",EDGE,"E10")])]})]}),makeQuery(id+"F16.opExtrude","SWEPT_FACE",FACE,{"disambiguationData":[OSD([subQ2]),TDD([subQ9])]})]}),makeQuery(id+"F20.opExtrude","SWEPT_FACE",FACE,{"disambiguationData":[OSD([subQ2]),TDD([makeQuery(id+"F16.boolean.opBoolean","COPY",EDGE,{"derivedFrom":makeQuery(id+"F16.opExtrude","CAP_EDGE",EDGE,{"disambiguationData":[OSD([subQ2]),TDD([subQ9])],"isStart":false})})])]})]}),makeQuery(id+"F20.boolean.opBoolean","MERGE",FACE,{"derivedFrom":[makeQuery(id+"F16.boolean.opBoolean","MERGE",FACE,{"derivedFrom":[makeQuery(id+"F13.boolean.opBoolean","MERGE",FACE,{"derivedFrom":[makeQuery(id+"F11.boolean.opBoolean","MERGE",FACE,{"derivedFrom":[subQ1,makeQuery(id+"F11.opExtrude","SWEPT_FACE",FACE,{"disambiguationData":[OSD([subQ6,subQ0])]})]}),makeQuery(id+"F13.opExtrude","SWEPT_FACE",FACE,{"disambiguationData":[OSD([subQ6,subQ0,subQ2,sQuery(id+"F2.wireOp",EDGE,"E12"),sQuery(id+"F10.wireOp",EDGE,"E17")])]})]}),makeQuery(id+"F16.opExtrude","SWEPT_FACE",FACE,{"disambiguationData":[OSD([subQ2]),TDD([subQ5])]})]}),makeQuery(id+"F20.opExtrude","SWEPT_FACE",FACE,{"disambiguationData":[OSD([subQ2]),TDD([makeQuery(id+"F16.boolean.opBoolean","COPY",EDGE,{"derivedFrom":makeQuery(id+"F16.opExtrude","CAP_EDGE",EDGE,{"disambiguationData":[OSD([subQ2]),TDD([subQ5])],"isStart":false})})])]})]}),makeQuery(id+"F27.opExtrude","SWEPT_FACE",FACE,{"disambiguationData":[OSD([sQuery(id+"F26.wireOp",EDGE,"E19.top")])]})]});}
            var sketch = newSketch(context, id + "F28", { "sketchPlane" : qUnion([Q0])});
            skCircle(sketch, "E20", {"center": v(0, 6) * mm, "radius": 1.5 * mm});
            skPoint(sketch, "E20.centerSnap0", {"position": v(0, 2.5) * mm});
            skCircle(sketch, "E21.0.1.0", {"center": v(0, 25) * mm, "radius": 1.5 * mm});
            skLineSegment(sketch, "E21.direction1", {"start": v(0, 6) * mm, "end": v(25, 6) * mm, "construction": true});
            skLineSegment(sketch, "E21.direction2", {"start": v(0, 6) * mm, "end": v(0, 25) * mm, "construction": true});
            skSolve(sketch);
        }
        {
            var Q0;
            Q0 = qSketchRegion(id + "F28", true);
            extrude(context, id + "F29", {"entities" : qUnion([Q0]), "operationType" : NewBodyOperationType.REMOVE, "oppositeDirection" : true, "depth" : 25 * mm});
        }
    });
